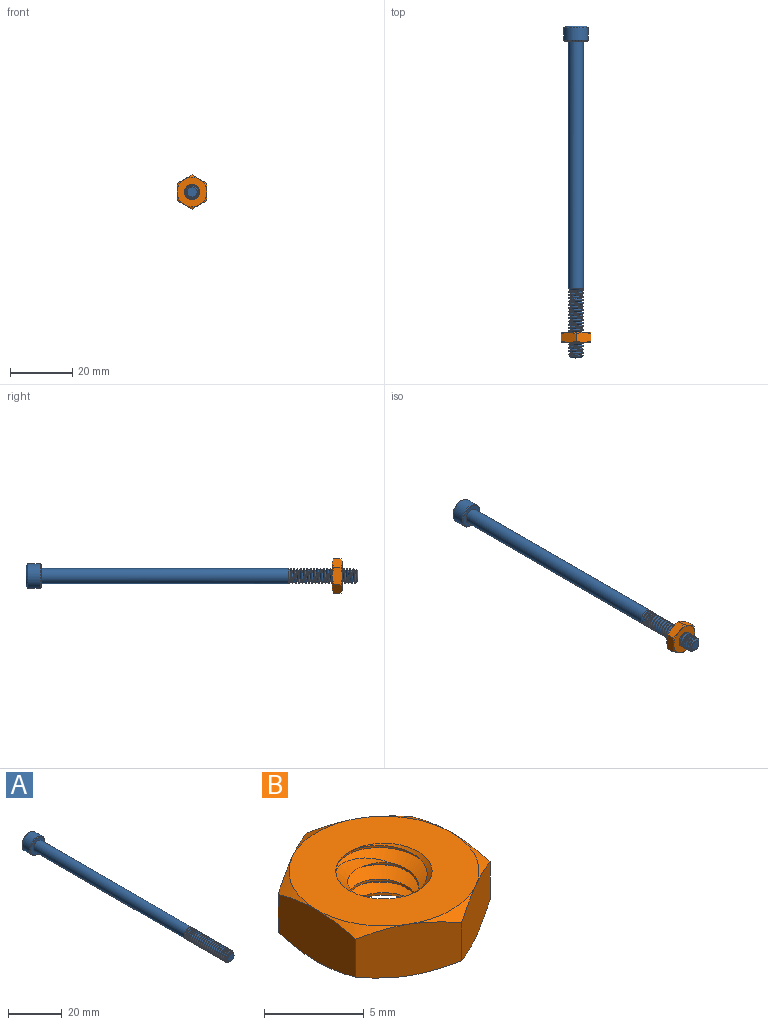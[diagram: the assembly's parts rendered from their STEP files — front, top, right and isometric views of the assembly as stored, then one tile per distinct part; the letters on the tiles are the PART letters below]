
ASSEMBLY  parts=2 mates=1
PART A: 46 faces, bbox 8.8x107.6x8.8 mm
  f0: cone r=3.96mm half-angle=45deg, axis (0,1,0), area 8.2mm2, adj f3,f33
  f1: cone r=3.48mm half-angle=45deg, axis (0,-1,0), area 16mm2, adj f3,f32
  f2: cone r=2.29mm half-angle=45deg, axis (0,1,0), area 0.5mm2, adj f32,f44
  f3: cylinder r=3.96mm len=7.92mm, axis (0,-1,0), area 102.1mm2, adj f0,f1
  f4: cone r=2.41mm half-angle=45deg, axis (0,1,0), area 6.6mm2, adj f27,f28,f29,f30
  f5: cone r=1.62mm half-angle=45deg, axis (0,1,0), area 7.6mm2, adj f7,f28,f29,f30,f31
  f6: cylinder r=2.41mm len=4.83mm, axis (0,-1,0), area 2mm2, adj f7,f8,f29,f30
  f7: cylinder r=2.41mm len=1.72mm, axis (0,-1,0), area 0.1mm2, adj f5,f6,f30
  f8: cylinder r=2.41mm len=4.83mm, axis (0,-1,0), area 2mm2, adj f6,f9,f29,f30
  f9: cylinder r=2.41mm len=4.83mm, axis (0,-1,0), area 2mm2, adj f8,f10,f29,f30
  f10: cylinder r=2.41mm len=4.83mm, axis (0,-1,0), area 2mm2, adj f9,f11,f29,f30
  f11: cylinder r=2.41mm len=4.83mm, axis (0,-1,0), area 2mm2, adj f10,f12,f29,f30
  f12: cylinder r=2.41mm len=4.83mm, axis (0,-1,0), area 2mm2, adj f11,f13,f29,f30
  f13: cylinder r=2.41mm len=4.83mm, axis (0,-1,0), area 2mm2, adj f12,f14,f29,f30
  f14: cylinder r=2.41mm len=4.83mm, axis (0,-1,0), area 2mm2, adj f13,f15,f29,f30
  f15: cylinder r=2.41mm len=4.83mm, axis (0,-1,0), area 2mm2, adj f14,f16,f29,f30
  f16: cylinder r=2.41mm len=4.83mm, axis (0,-1,0), area 2mm2, adj f15,f17,f29,f30
  f17: cylinder r=2.41mm len=4.83mm, axis (0,-1,0), area 2mm2, adj f16,f18,f29,f30
  f18: cylinder r=2.41mm len=4.83mm, axis (0,-1,0), area 2mm2, adj f17,f19,f29,f30
  f19: cylinder r=2.41mm len=4.83mm, axis (0,-1,0), area 2mm2, adj f18,f20,f29,f30
  f20: cylinder r=2.41mm len=4.83mm, axis (0,-1,0), area 2mm2, adj f19,f21,f29,f30
  f21: cylinder r=2.41mm len=4.83mm, axis (0,-1,0), area 2mm2, adj f20,f22,f29,f30
  f22: cylinder r=2.41mm len=4.83mm, axis (0,-1,0), area 2mm2, adj f21,f23,f29,f30
  f23: cylinder r=2.41mm len=4.83mm, axis (0,-1,0), area 2mm2, adj f22,f24,f29,f30
  f24: cylinder r=2.41mm len=4.83mm, axis (0,-1,0), area 2mm2, adj f23,f25,f29,f30
  f25: cylinder r=2.41mm len=4.83mm, axis (0,-1,0), area 2mm2, adj f24,f26,f29,f30
  f26: cylinder r=2.41mm len=4.83mm, axis (0,-1,0), area 2mm2, adj f25,f27,f29,f30
  f27: cylinder r=2.41mm len=79.64mm, axis (0,-1,0), area 1203.8mm2, adj f4,f26,f29,f30,f33
  f28: cylinder r=1.73mm len=21.43mm, axis (0,1,0), area 29mm2, adj f4,f5,f29,f30
  f29: bspline ~22.12x4.83mm, area 209.5mm2, adj f4,f5,f6,f8,f9,f10,f11,f12
  f30: bspline ~22.91x4.82mm, area 210mm2, adj f4,f5,f6,f7,f8,f9,f10,f11
  f31: plane 3.24x3.24mm, normal (0,-1,0), area 8.2mm2, adj f5
  f32: plane 7.71x7.71mm, normal (0,1,0), area 21.5mm2, adj f1,f2,f34,f35,f36,f37,f38
  f33: plane 7.44x7.44mm, normal (0,-1,0), area 25.2mm2, adj f0,f27
  f34: cone r=2.29mm half-angle=45deg, axis (0,1,0), area 0mm2, adj f32,f40
  f35: cone r=2.29mm half-angle=45deg, axis (0,1,0), area 0mm2, adj f32,f41
  f36: cone r=2.29mm half-angle=45deg, axis (0,1,0), area 0mm2, adj f32,f42
  f37: cone r=2.29mm half-angle=45deg, axis (0,1,0), area 0mm2, adj f32,f43
  f38: cone r=2.29mm half-angle=45deg, axis (0,1,0), area 0mm2, adj f32,f45
  f39: plane 4.58x3.97mm, normal (0,1,0), area 13.6mm2, adj f40,f41,f42,f43,f44,f45
  f40: plane 3.84x2.85mm, normal (-0.5,0,-0.87), area 6.4mm2, adj f34,f39,f41,f45
  f41: plane 3.84x3.16mm, normal (-1,0,0), area 6.4mm2, adj f35,f39,f40,f42
  f42: plane 3.84x2.85mm, normal (-0.5,0,0.87), area 6.4mm2, adj f36,f39,f41,f43
  f43: plane 3.84x2.85mm, normal (0.5,0,0.87), area 6.4mm2, adj f37,f39,f42,f44
  f44: plane 3.2x2.51mm, normal (1,0,0), area 6.4mm2, adj f2,f39,f43,f45
  f45: plane 3.84x2.85mm, normal (0.5,0,-0.87), area 6.4mm2, adj f38,f39,f40,f44
PART B: 26 faces, bbox 11.5x11.5x4.4 mm
  f0: cone r=4.76mm half-angle=60deg, axis (0,0,1), area 2.2mm2, adj f11,f12,f15
  f1: cone r=2.41mm half-angle=45deg, axis (0,0,-1), area 6.6mm2, adj f5,f6,f7,f15
  f2: cone r=4.76mm half-angle=60deg, axis (0,0,-1), area 2.2mm2, adj f8,f11,f12
  f3: cone r=2.41mm half-angle=45deg, axis (0,0,1), area 6.6mm2, adj f5,f6,f7,f8
  f4: cylinder r=2.41mm len=4.83mm, axis (0,0,-1), area 6mm2, adj f5,f7,f8,f15
  f5: bspline ~4.83x4.83mm, area 24.7mm2, adj f1,f3,f4,f6
  f6: cylinder r=1.73mm len=3.45mm, axis (0,0,-1), area 2.4mm2, adj f1,f3,f5,f7
  f7: bspline ~4.83x4.83mm, area 24.9mm2, adj f1,f3,f4,f6
  f8: plane 9.53x9.53mm, normal (0,0,1), area 53mm2, adj f2,f3,f4,f16,f17,f18,f19,f20
  f9: plane 5.21x3.63mm, normal (-0.5,0.87,0), area 15.9mm2, adj f10,f14,f16,f20,f23,f24
  f10: plane 5.95x3.63mm, normal (-1,0,0), area 15.9mm2, adj f9,f11,f19,f20,f24,f25
  f11: plane 5.21x3.63mm, normal (-0.5,-0.87,0), area 15.9mm2, adj f0,f2,f10,f12,f19,f25
  f12: plane 5.21x3.63mm, normal (0.5,-0.87,0), area 15.8mm2, adj f0,f2,f11,f13,f18,f21
  f13: plane 5.95x3.63mm, normal (1,0,0), area 15.9mm2, adj f12,f14,f17,f18,f21,f22
  f14: plane 5.21x3.63mm, normal (0.5,0.87,0), area 15.9mm2, adj f9,f13,f16,f17,f22,f23
  f15: plane 9.53x9.53mm, normal (0,0,-1), area 53mm2, adj f0,f1,f4,f21,f22,f23,f24,f25
  f16: cone r=4.76mm half-angle=60deg, axis (0,0,-1), area 2.2mm2, adj f8,f9,f14
  f17: cone r=4.76mm half-angle=60deg, axis (0,0,-1), area 2.2mm2, adj f8,f13,f14
  f18: cone r=4.76mm half-angle=60deg, axis (0,0,-1), area 2.2mm2, adj f8,f12,f13
  f19: cone r=4.76mm half-angle=60deg, axis (0,0,-1), area 2.2mm2, adj f8,f10,f11
  f20: cone r=4.76mm half-angle=60deg, axis (0,0,-1), area 2.2mm2, adj f8,f9,f10
  f21: cone r=4.76mm half-angle=60deg, axis (0,0,1), area 2.2mm2, adj f12,f13,f15
  f22: cone r=4.76mm half-angle=60deg, axis (0,0,1), area 2.2mm2, adj f13,f14,f15
  f23: cone r=4.76mm half-angle=60deg, axis (0,0,1), area 2.2mm2, adj f9,f14,f15
  f24: cone r=4.76mm half-angle=60deg, axis (0,0,1), area 2.2mm2, adj f9,f10,f15
  f25: cone r=4.76mm half-angle=60deg, axis (0,0,1), area 2.2mm2, adj f10,f11,f15
PLACE A rot(axis=(0,-1,0),98.3deg) t=(-89.54,-39.65,5.8)mm
PLACE B rot(axis=(1,0,0),90deg) t=(-89.54,-33.05,5.8)mm
MATE cylindrical B.f0 <-> A.f0  axis (0,-1,0) through (-89.54,-34.64,5.8)mm
